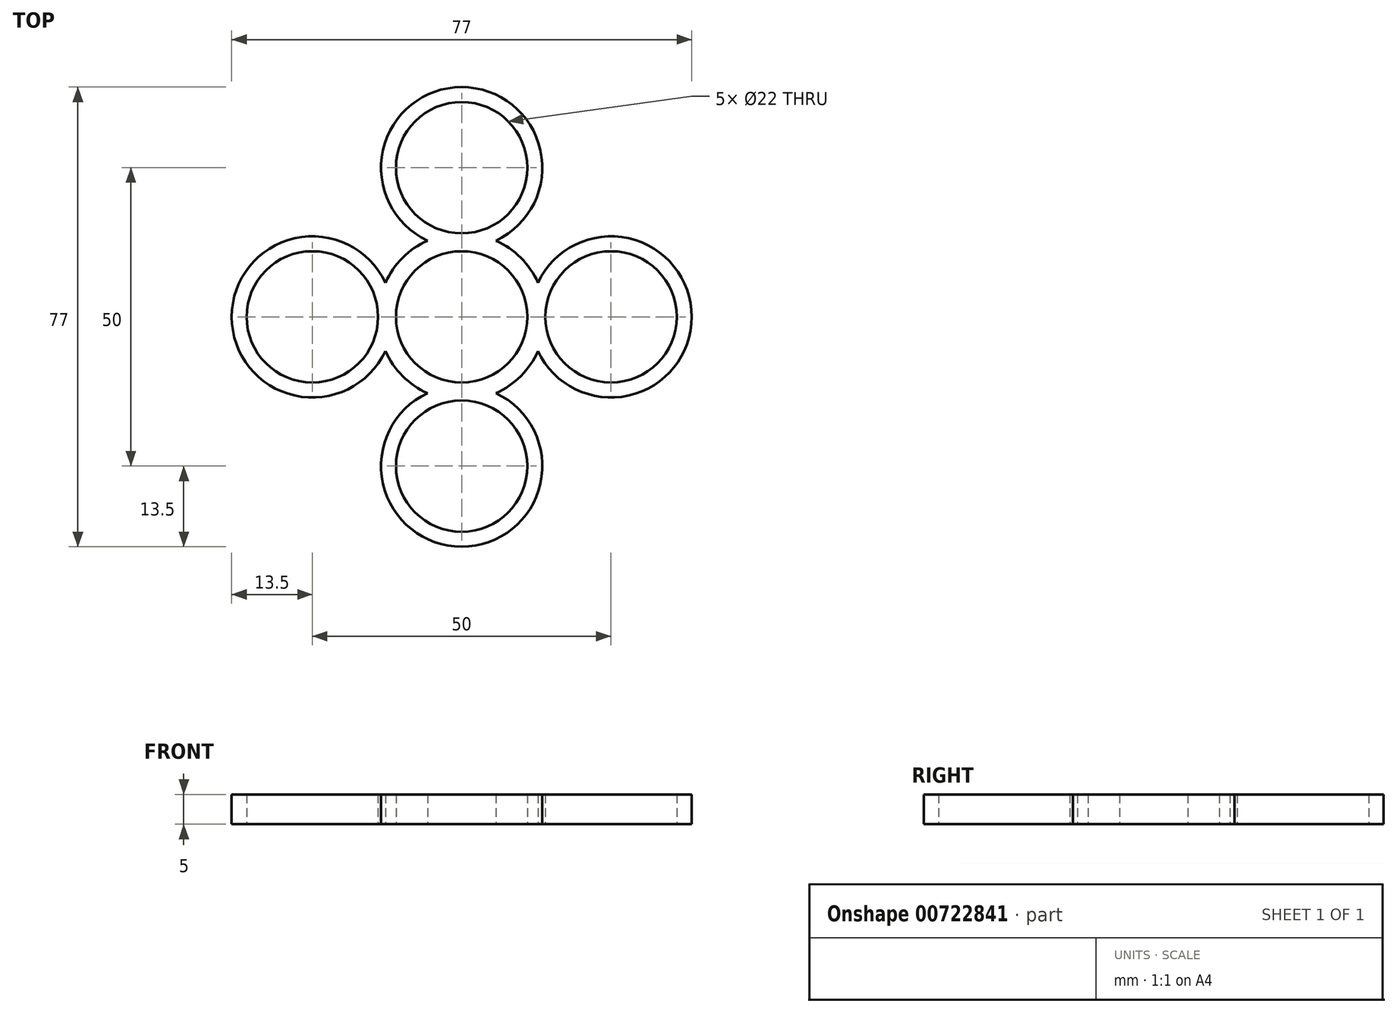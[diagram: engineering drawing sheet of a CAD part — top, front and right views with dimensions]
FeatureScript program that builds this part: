
annotation { "Feature Type Name" : "Feature", "Feature Type Description" : "" }
export const myFeature = defineFeature(function(context is Context, id is Id, definition is map)
    precondition{}
    {
        {
            var Q0;
            Q0=qCreatedBy(makeId("Top.planeOp"),FACE);
            var sketch = newSketch(context, id + "F0", { "sketchPlane" : qUnion([Q0])});
            skCircle(sketch, "E0", {"center": v(0, 0) * mm, "radius": 11 * mm});
            skCircle(sketch, "E1", {"center": v(0, 25) * mm, "radius": 11 * mm});
            skArc(sketch, "E2", {"start": v(-5.73, 12.78) * mm, "mid": v(-9.9, 9.9) * mm, "end": v(-12.77, 5.73) * mm});
            skArc(sketch, "E3", {"start": v(5.73, 12.77) * mm, "mid": v(0, 38.5) * mm, "end": v(-5.73, 12.78) * mm});
            skCircle(sketch, "E4", {"center": v(0, -25) * mm, "radius": 11 * mm});
            skArc(sketch, "E5", {"start": v(-5.73, -12.78) * mm, "mid": v(0, -38.5) * mm, "end": v(5.73, -12.78) * mm});
            skArc(sketch, "E6.trimOffspring", {"start": v(5.73, -12.78) * mm, "mid": v(9.9, -9.9) * mm, "end": v(12.78, -5.73) * mm});
            skCircle(sketch, "E7", {"center": v(-25, 0) * mm, "radius": 11 * mm});
            skPoint(sketch, "E8.endSnap0", {"position": v(14, 0) * mm});
            skCircle(sketch, "E9", {"center": v(25, 0) * mm, "radius": 11 * mm});
            skArc(sketch, "E10", {"start": v(-12.77, 5.73) * mm, "mid": v(-38.5, 0) * mm, "end": v(-12.78, -5.73) * mm});
            skArc(sketch, "E11", {"start": v(12.78, -5.73) * mm, "mid": v(38.5, 0) * mm, "end": v(12.78, 5.73) * mm});
            skArc(sketch, "E12.trimOffspring", {"start": v(-12.77, -5.73) * mm, "mid": v(-9.9, -9.9) * mm, "end": v(-5.73, -12.78) * mm});
            skArc(sketch, "E13.trimOffspring", {"start": v(12.78, 5.73) * mm, "mid": v(9.9, 9.9) * mm, "end": v(5.73, 12.78) * mm});
            skSolve(sketch);
        }
        {
            var Q0;
            Q0=makeQuery(id+"F0.imprint","IMPRINT",FACE,{"disambiguationData":[TD([[makeQuery(id+"F0.imprint","IMPRINT",EDGE,{"derivedFrom":sQuery(id+"F0.wireOp",EDGE,"E0")}),-1.0]])]});
            extrude(context, id + "F1", {"entities" : qUnion([Q0]), "depth" : 5 * mm, "offsetDistance" : 25 * mm});
        }
    });
